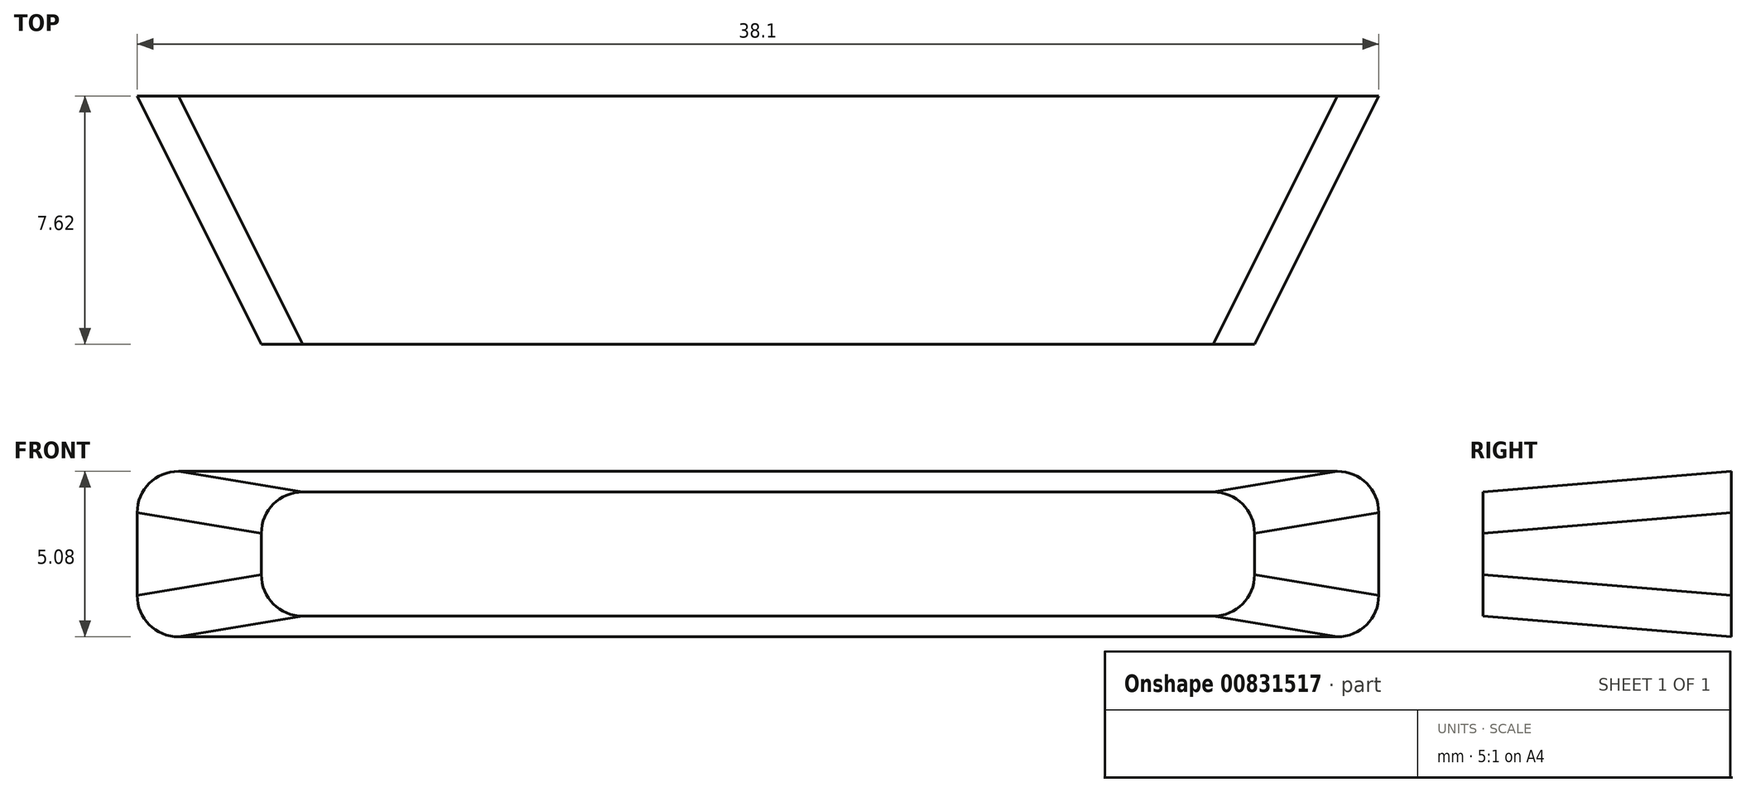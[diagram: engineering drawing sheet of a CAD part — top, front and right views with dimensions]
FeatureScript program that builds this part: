
annotation { "Feature Type Name" : "Feature", "Feature Type Description" : "" }
export const myFeature = defineFeature(function(context is Context, id is Id, definition is map)
    precondition{}
    {
        {
            var Q0;
            Q0=qCreatedBy(makeId("Front.planeOp"),FACE);
            var sketch = newSketch(context, id + "F0", { "sketchPlane" : qUnion([Q0])});
            skLineSegment(sketch, "E0.bottom", {"start": v(17.78, 2.54) * mm, "end": v(-17.78, 2.54) * mm});
            skLineSegment(sketch, "E0.top", {"start": v(17.78, -2.54) * mm, "end": v(-17.78, -2.54) * mm});
            skLineSegment(sketch, "E0.left", {"start": v(19.05, 1.27) * mm, "end": v(19.05, -1.27) * mm});
            skLineSegment(sketch, "E0.right", {"start": v(-19.05, 1.27) * mm, "end": v(-19.05, -1.27) * mm});
            skPoint(sketch, "E0.middle", {"position": v(0, 0) * mm});
            skPoint(sketch, "E1.visualSharp", {"position": v(-19.05, 2.54) * mm});
            skArc(sketch, "E1.filletArc", {"start": v(-17.78, 2.54) * mm, "mid": v(-18.68, 2.17) * mm, "end": v(-19.05, 1.27) * mm});
            skPoint(sketch, "E2.visualSharp", {"position": v(19.05, 2.54) * mm});
            skArc(sketch, "E2.filletArc", {"start": v(19.05, 1.27) * mm, "mid": v(18.68, 2.17) * mm, "end": v(17.78, 2.54) * mm});
            skPoint(sketch, "E3.visualSharp", {"position": v(19.05, -2.54) * mm});
            skArc(sketch, "E3.filletArc", {"start": v(17.78, -2.54) * mm, "mid": v(18.68, -2.17) * mm, "end": v(19.05, -1.27) * mm});
            skPoint(sketch, "E4.visualSharp", {"position": v(-19.05, -2.54) * mm});
            skArc(sketch, "E4.filletArc", {"start": v(-19.05, -1.27) * mm, "mid": v(-18.68, -2.17) * mm, "end": v(-17.78, -2.54) * mm});
            skSolve(sketch);
        }
        {
            var Q0;
            Q0=qCreatedBy(makeId("Front.planeOp"),FACE);
            cPlane(context, id + "F1", {"entities" : qUnion([Q0]), "cplaneType" : CPlaneType.OFFSET, "offset" : 7.62 * mm, "width" : 152.4 * mm, "height" : 152.4 * mm});
        }
        {
            var Q0;
            Q0=qCreatedBy(id+"F1.planeOp",FACE);
            var sketch = newSketch(context, id + "F2", { "sketchPlane" : qUnion([Q0])});
            skLineSegment(sketch, "E5.bottom", {"start": v(13.97, 1.9) * mm, "end": v(-13.97, 1.9) * mm});
            skLineSegment(sketch, "E5.top", {"start": v(13.97, -1.9) * mm, "end": v(-13.97, -1.9) * mm});
            skLineSegment(sketch, "E5.left", {"start": v(15.24, 0.63) * mm, "end": v(15.24, -0.63) * mm});
            skLineSegment(sketch, "E5.right", {"start": v(-15.24, 0.64) * mm, "end": v(-15.24, -0.63) * mm});
            skPoint(sketch, "E5.middle", {"position": v(0, 0) * mm});
            skPoint(sketch, "E6.visualSharp", {"position": v(-15.24, 1.9) * mm});
            skArc(sketch, "E6.filletArc", {"start": v(-13.97, 1.9) * mm, "mid": v(-14.87, 1.53) * mm, "end": v(-15.24, 0.64) * mm});
            skPoint(sketch, "E7.visualSharp", {"position": v(-15.24, -1.9) * mm});
            skArc(sketch, "E7.filletArc", {"start": v(-15.24, -0.63) * mm, "mid": v(-14.87, -1.53) * mm, "end": v(-13.97, -1.9) * mm});
            skPoint(sketch, "E8.visualSharp", {"position": v(15.24, -1.9) * mm});
            skArc(sketch, "E8.filletArc", {"start": v(13.97, -1.9) * mm, "mid": v(14.87, -1.53) * mm, "end": v(15.24, -0.63) * mm});
            skPoint(sketch, "E9.visualSharp", {"position": v(15.24, 1.9) * mm});
            skArc(sketch, "E9.filletArc", {"start": v(15.24, 0.63) * mm, "mid": v(14.87, 1.53) * mm, "end": v(13.97, 1.9) * mm});
            skSolve(sketch);
        }
        {
            var Q0;
            {var subQ1=sQuery(id+"F0.wireOp",EDGE,"E0.bottom");Q0=makeQuery(id+"F0.imprint","IMPRINT",FACE,{"disambiguationData":[TD([[makeQuery(id+"F0.imprint","IMPRINT",EDGE,{"derivedFrom":subQ1}),1.0]])]});}
            var Q1;
            Q1=makeQuery(id+"F2.imprint","IMPRINT",FACE,{"disambiguationData":[TD([[makeQuery(id+"F2.imprint","IMPRINT",EDGE,{"derivedFrom":sQuery(id+"F2.wireOp",EDGE,"E5.bottom")}),1.0]])]});
            loft(context, id + "F3", {"sheetProfilesArray" : [{ "sheetProfileEntities" : qUnion([Q0]) }, { "sheetProfileEntities" : qUnion([Q1]) }]});
        }
    });
